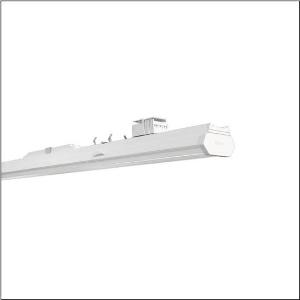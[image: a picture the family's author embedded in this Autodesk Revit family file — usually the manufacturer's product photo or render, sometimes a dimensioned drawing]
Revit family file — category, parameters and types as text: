
# Revit family: licross_r__11_protected_ho_51tp12dn4fxm3s4_aaf8
name_source: partatom
category: Lighting Fixtures
units: mm (PartAtom-declared; Revit-internal decimal feet)

## family parameters
Cut with Voids When Loaded = No
Host = Face
Light Source = No
Part Type = Normal
Room Calculation Point = No
Round Connector Dimension = Use Diameter
Shared = No

## types (1)
- --- (1 x LED, 970 lm, 7.4 W, 4000K)
    Apparent Load = 7 VA
    CIE Flux Codes = 70 91 97 98 100
    Color Rendering = 80
    Color Temperature = 4000K
    Default Elevation = 1800 mm
    Description = Licross® 11 Protected HO, luminaire insert, of sheet steel, galvanised, coil coated, white, length: 1.500mm, width: 90mm, height: 101mm, LED rated luminous flux: 15.270lm, light colour: 840, control gear: DALI 2, with plug, 6-pole, with phase selection, for trunking rail, 9 or 11-core, mains connection: 220..240V, AC, 50/60Hz, rated input power: 91W, for trunking rail, 9-/11-core, halogen-free wiring, for emergency light function, converter,control gear: single battery element, battery: LiFeP04, 9Ah, primary light control with lens, of plastic, primary optical cover: cover, of PMMA, light emission: direct distribution, primary light characteristic: symmetric, protection rating (complete): IP64, insulation class (complete): insulation class I (protective earthing), certification: CE, UKCA, protection symbol: D if used in an environment with conductive dust loads with corresponding accessories, impact resistance: IK06, permissible ambient temperature for indoor applications: +5..+30°C, standard: EN 60598-2-22, LABS conformity tested according to VDMA 24364:2018-05, reducing of maximum allowable ambient temperature of 5°C with ceiling mounting, corresponds to IFS (International Featured Standards) requirements for safety and quality in the food industry, packaging unit: 1 piece
    Height = 92 mm
    Lamp = 1 x LED
    Lamp Light Flux = 970 lm
    Lamp Power = 7.4 W
    Lamp count = 1
    Length = 1500 mm
    Luminous efficacy = 131 lm/W
    Manufacturer = Siteco
    ModVariant = No
    Model = 51TP12DN4FXM3S4
    Mounting Place = Ceiling
    Mounting Type = Pendant
    Number of Poles = 1
    OnlyDefault = Yes
    Power Factor = 1
    Product Name = Licross® 11 Protected HO
    Product group = luminaire insert
    ProductGroupID = 901
    Protection Class = Protection class I
    Protection Degree = IP 64
    RLX_Detail_Level = 1
    RLX_Emergency_Light_Flux = 0 lm
    RLX_Emergency_Type = 0
    RLX_Emergency_Type_DB = No
    RlxData = <blob elided: 24997 chars, md5=f73e6a3c>
    Socket = socket
    Standby Power = 0 W
    System Light Flux = 970 lm
    System Power = 7 W
    Type Comments = : emergency light operation: 3 h
    Type Image = l_1256148.jpg
    URL = http://relux.com
    VarID = @adj_041391
    Voltage = 0 V
    Weight = 0.00 kg
    Width = 88 mm

## geometry (parser evidence)
native form markers: Blend x4, Sweep x10
no freeform markers — native parametric forms only
